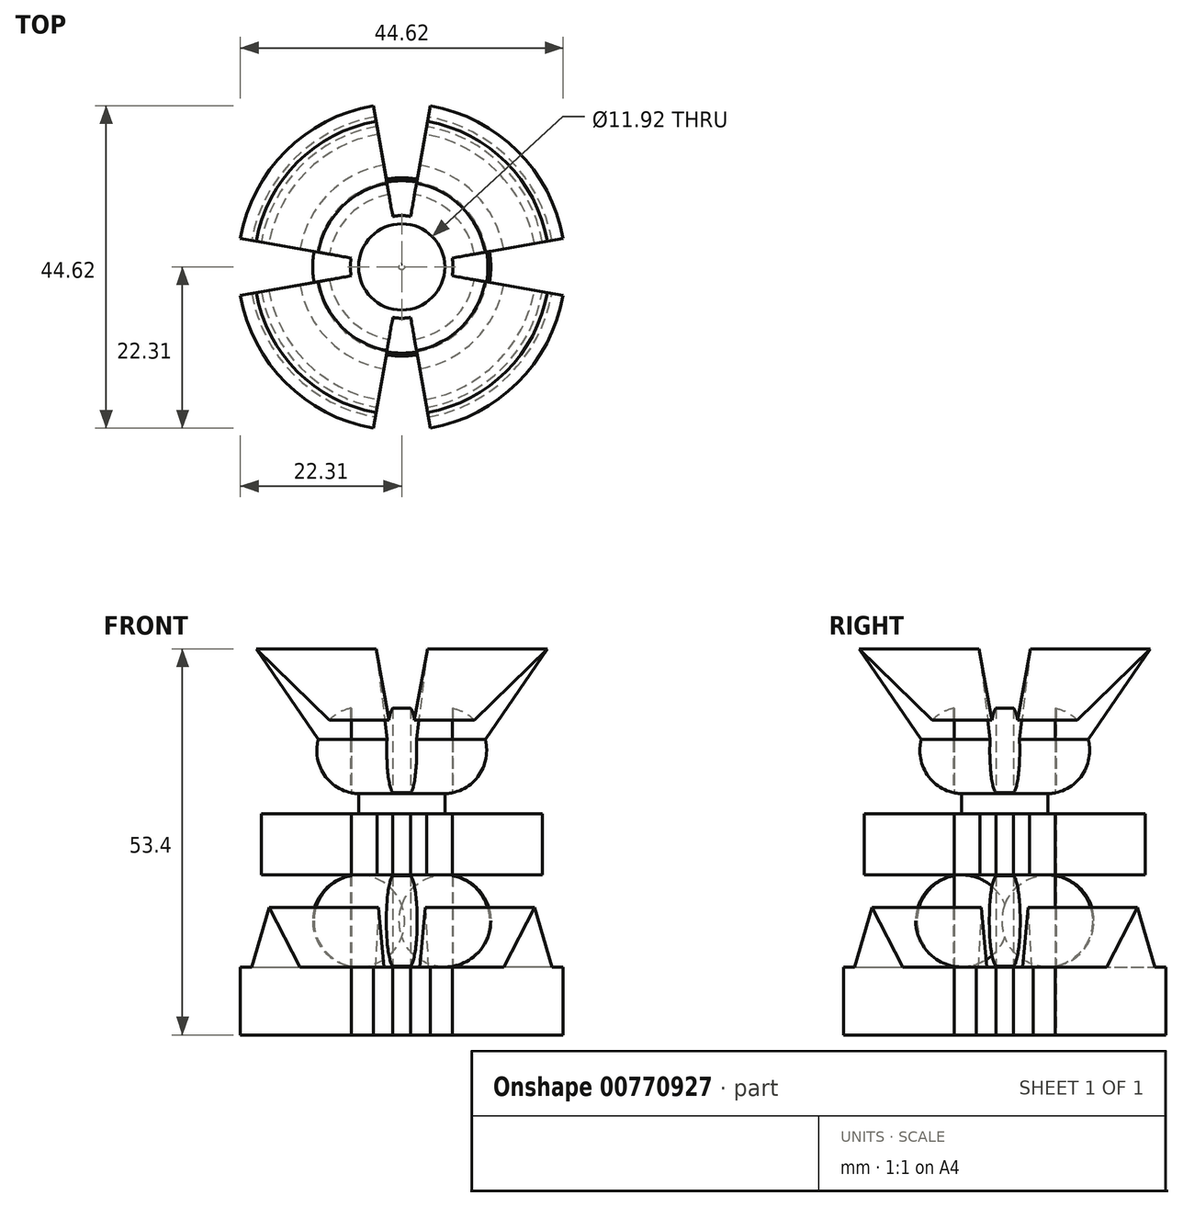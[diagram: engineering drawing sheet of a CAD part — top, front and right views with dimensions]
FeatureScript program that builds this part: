
annotation { "Feature Type Name" : "Feature", "Feature Type Description" : "" }
export const myFeature = defineFeature(function(context is Context, id is Id, definition is map)
    precondition{}
    {
        {
            var Q0;
            Q0=qCreatedBy(makeId("Front.planeOp"),FACE);
            var sketch = newSketch(context, id + "F0", { "sketchPlane" : qUnion([Q0])});
            skLineSegment(sketch, "E0.bottom", {"start": v(0, 0) * mm, "end": v(22.65, 0) * mm});
            skLineSegment(sketch, "E0.top", {"start": v(5.96, 9.4) * mm, "end": v(14.3, 9.4) * mm});
            skLineSegment(sketch, "E0.left", {"start": v(0, 0) * mm, "end": v(0, 9.4) * mm});
            skLineSegment(sketch, "E0.right", {"start": v(22.65, 0) * mm, "end": v(22.65, 9.4) * mm});
            skLineSegment(sketch, "E1.right", {"start": v(0, 9.4) * mm, "end": v(0, 39.34) * mm});
            skLineSegment(sketch, "E2.bottom", {"start": v(5.96, 30.6) * mm, "end": v(19.74, 30.6) * mm});
            skLineSegment(sketch, "E2.top", {"start": v(5.96, 22.12) * mm, "end": v(19.74, 22.12) * mm});
            skLineSegment(sketch, "E2.right", {"start": v(19.74, 30.6) * mm, "end": v(19.74, 22.12) * mm});
            skArc(sketch, "E3", {"start": v(5.96, 33.38) * mm, "mid": v(10.68, 35.7) * mm, "end": v(11.73, 40.86) * mm});
            skLineSegment(sketch, "E4.trimOffspring", {"start": v(5.96, 30.6) * mm, "end": v(5.96, 33.38) * mm});
            skLineSegment(sketch, "E5", {"start": v(10.18, 43.56) * mm, "end": v(20.44, 53.4) * mm});
            skLineSegment(sketch, "E6", {"start": v(20.44, 53.4) * mm, "end": v(11.73, 40.86) * mm});
            skArc(sketch, "E7.trimOffspring", {"start": v(10.18, 43.56) * mm, "mid": v(3.68, 44.85) * mm, "end": v(0, 39.34) * mm});
            skArc(sketch, "E8", {"start": v(5.96, 9.4) * mm, "mid": v(12.32, 15.76) * mm, "end": v(5.96, 22.12) * mm});
            skLineSegment(sketch, "E9", {"start": v(14.3, 9.4) * mm, "end": v(18.64, 17.6) * mm});
            skLineSegment(sketch, "E10", {"start": v(18.64, 17.6) * mm, "end": v(21.08, 9.4) * mm});
            skLineSegment(sketch, "E11.trimOffspring", {"start": v(21.08, 9.4) * mm, "end": v(22.65, 9.4) * mm});
            skSolve(sketch);
        }
        {
            var Q0;
            Q0=makeQuery(id+"F0.imprint","IMPRINT",FACE,{"disambiguationData":[TD([[makeQuery(id+"F0.imprint","IMPRINT",EDGE,{"derivedFrom":sQuery(id+"F0.wireOp",EDGE,"E0.bottom")}),1.0]])]});
            var Q1;
            Q1=sQuery(id+"F0.wireOp",EDGE,"E1.right");
            revolve(context, id + "F1", {"surfaceOperationType" : NewSurfaceOperationType.NEW, "entities" : qUnion([Q0]), "axis" : qUnion([Q1]), "revolveType" : RevolveType.FULL});
        }
        {
            var Q0;
            Q0=qCreatedBy(makeId("Top.planeOp"),FACE);
            var sketch = newSketch(context, id + "F2", { "sketchPlane" : qUnion([Q0])});
            skLineSegment(sketch, "E12", {"start": v(1.23, 6.99) * mm, "end": v(5.7, 32.38) * mm});
            skLineSegment(sketch, "E13", {"start": v(-1.23, 6.99) * mm, "end": v(-5.7, 32.38) * mm});
            skArc(sketch, "E14", {"start": v(1.23, 6.99) * mm, "mid": v(0, 7.1) * mm, "end": v(-1.23, 6.99) * mm});
            skArc(sketch, "E15", {"start": v(5.7, 32.38) * mm, "mid": v(0, 32.88) * mm, "end": v(-5.7, 32.38) * mm});
            skLineSegment(sketch, "E16.1.0", {"start": v(-6.99, -1.23) * mm, "end": v(-32.38, -5.7) * mm});
            skArc(sketch, "E16.1.1", {"start": v(-32.38, 5.7) * mm, "mid": v(-32.88, 0) * mm, "end": v(-32.38, -5.7) * mm});
            skLineSegment(sketch, "E16.1.2", {"start": v(-6.99, 1.23) * mm, "end": v(-32.38, 5.7) * mm});
            skArc(sketch, "E16.1.3", {"start": v(-6.99, 1.23) * mm, "mid": v(-7.1, 0) * mm, "end": v(-6.99, -1.23) * mm});
            skLineSegment(sketch, "E16.2.0", {"start": v(1.23, -6.99) * mm, "end": v(5.7, -32.38) * mm});
            skArc(sketch, "E16.2.1", {"start": v(-5.7, -32.38) * mm, "mid": v(0, -32.88) * mm, "end": v(5.7, -32.38) * mm});
            skLineSegment(sketch, "E16.2.2", {"start": v(-1.23, -6.99) * mm, "end": v(-5.7, -32.38) * mm});
            skArc(sketch, "E16.2.3", {"start": v(-1.23, -6.99) * mm, "mid": v(0, -7.1) * mm, "end": v(1.23, -6.99) * mm});
            skLineSegment(sketch, "E16.3.0", {"start": v(6.99, 1.23) * mm, "end": v(32.38, 5.7) * mm});
            skArc(sketch, "E16.3.1", {"start": v(32.38, -5.7) * mm, "mid": v(32.88, 0) * mm, "end": v(32.38, 5.7) * mm});
            skLineSegment(sketch, "E16.3.2", {"start": v(6.99, -1.23) * mm, "end": v(32.38, -5.7) * mm});
            skArc(sketch, "E16.3.3", {"start": v(6.99, -1.23) * mm, "mid": v(7.1, 0) * mm, "end": v(6.99, 1.23) * mm});
            skSolve(sketch);
        }
        {
            var Q0;
            Q0=makeQuery(id+"F2.imprint","IMPRINT",FACE,{"disambiguationData":[TD([[makeQuery(id+"F2.imprint","IMPRINT",EDGE,{"derivedFrom":sQuery(id+"F2.wireOp",EDGE,"E16.1.0")}),-1.0]])]});
            var Q1;
            Q1=makeQuery(id+"F2.imprint","IMPRINT",FACE,{"disambiguationData":[TD([[makeQuery(id+"F2.imprint","IMPRINT",EDGE,{"derivedFrom":sQuery(id+"F2.wireOp",EDGE,"E16.2.0")}),-1.0]])]});
            var Q2;
            Q2=makeQuery(id+"F2.imprint","IMPRINT",FACE,{"disambiguationData":[TD([[makeQuery(id+"F2.imprint","IMPRINT",EDGE,{"derivedFrom":sQuery(id+"F2.wireOp",EDGE,"E16.3.0")}),-1.0]])]});
            var Q3;
            Q3=makeQuery(id+"F2.imprint","IMPRINT",FACE,{"disambiguationData":[TD([[makeQuery(id+"F2.imprint","IMPRINT",EDGE,{"derivedFrom":sQuery(id+"F2.wireOp",EDGE,"E12")}),1.0]])]});
            extrude(context, id + "F3", {"entities" : qUnion([Q0, Q1, Q2, Q3]), "operationType" : NewBodyOperationType.REMOVE, "depth" : 86.3 * mm, "offsetDistance" : 25 * mm});
        }
    });
